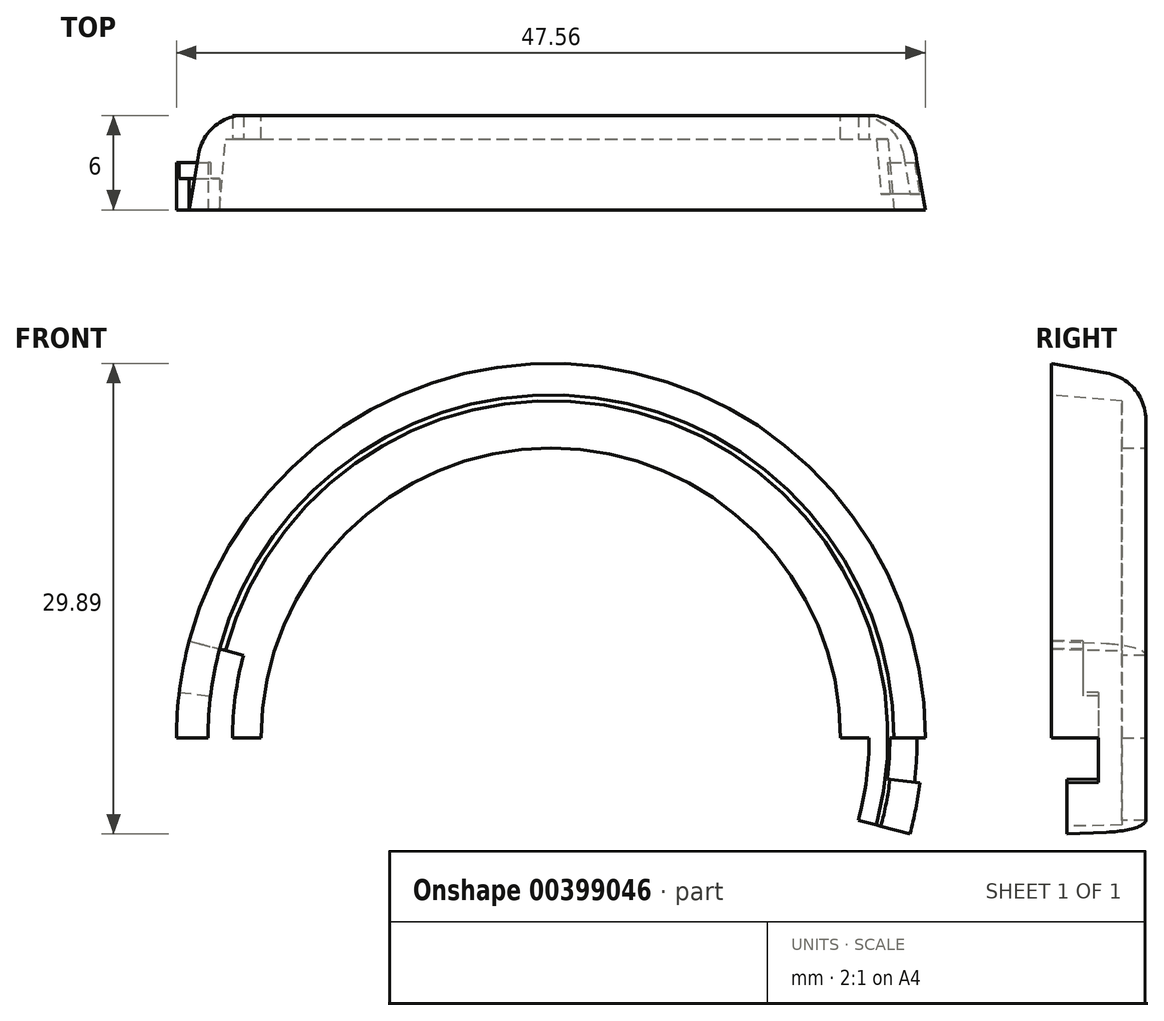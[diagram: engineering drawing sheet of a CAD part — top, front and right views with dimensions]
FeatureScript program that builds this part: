
annotation { "Feature Type Name" : "Feature", "Feature Type Description" : "" }
export const myFeature = defineFeature(function(context is Context, id is Id, definition is map)
    precondition{}
    {
        {
            var Q0;
            Q0=qCreatedBy(makeId("Top.planeOp"),FACE);
            var sketch = newSketch(context, id + "F0", { "sketchPlane" : qUnion([Q0])});
            skLineSegment(sketch, "E0", {"start": v(0, 0) * mm, "end": v(0, -13.08) * mm, "construction": true});
            skLineSegment(sketch, "E1", {"start": v(18.4, 6) * mm, "end": v(18.4, 4.5) * mm});
            skLineSegment(sketch, "E2", {"start": v(18.4, 6) * mm, "end": v(22.74, 6) * mm});
            skLineSegment(sketch, "E3", {"start": v(22.74, 6) * mm, "end": v(23.78, 0) * mm});
            skLineSegment(sketch, "E4", {"start": v(23.78, 0) * mm, "end": v(21.78, 0) * mm});
            skLineSegment(sketch, "E5", {"start": v(21.78, 0) * mm, "end": v(21.4, 4.5) * mm});
            skLineSegment(sketch, "E6", {"start": v(21.4, 4.5) * mm, "end": v(18.4, 4.5) * mm});
            skSolve(sketch);
        }
        {
            var Q0;
            Q0 = qSketchRegion(id + "F0", true);
            var Q1;
            Q1=sQuery(id+"F0.wireOp",EDGE,"E0");
            revolve(context, id + "F1", {"entities" : qUnion([Q0]), "axis" : qUnion([Q1]), "revolveType" : RevolveType.FULL});
        }
        {
            var Q0;
            Q0=makeQuery(id+"F1.opRevolve","SWEPT_EDGE",EDGE,{"disambiguationData":[OSD([sQuery(id+"F0.wireOp",EDGE,"E2"),sQuery(id+"F0.wireOp",EDGE,"E3")])]});
            fillet(context, id + "F2", {"entities" : qUnion([Q0]), "radius" : 3 * mm, "tangentPropagation" : true, "allowEdgeOverflow" : false});
        }
        {
            var Q0;
            Q0=qCreatedBy(makeId("Front.planeOp"),FACE);
            var sketch = newSketch(context, id + "F3", { "sketchPlane" : qUnion([Q0])});
            skLineSegment(sketch, "E7", {"start": v(-26.64, 7.14) * mm, "end": v(-19.53, 5.23) * mm});
            skLineSegment(sketch, "E8", {"start": v(-20.21, 0) * mm, "end": v(0, 0) * mm});
            skLineSegment(sketch, "E9", {"start": v(0, 0) * mm, "end": v(20.21, 0) * mm});
            skLineSegment(sketch, "E10", {"start": v(19.53, -5.23) * mm, "end": v(26.77, -7.17) * mm});
            skLineSegment(sketch, "E11", {"start": v(-26.64, 7.14) * mm, "end": v(-26.64, -27.7) * mm});
            skLineSegment(sketch, "E12", {"start": v(-26.64, -27.7) * mm, "end": v(26.77, -27.7) * mm});
            skLineSegment(sketch, "E13", {"start": v(26.77, -27.7) * mm, "end": v(26.77, -7.17) * mm});
            skLineSegment(sketch, "E14", {"start": v(-19.53, 5.23) * mm, "end": v(0, 0) * mm, "construction": true});
            skArc(sketch, "E15", {"start": v(-19.53, 5.23) * mm, "mid": v(-20.04, 2.64) * mm, "end": v(-20.21, 0) * mm});
            skLineSegment(sketch, "E16", {"start": v(0, 0) * mm, "end": v(19.53, -5.23) * mm, "construction": true});
            skArc(sketch, "E17", {"start": v(19.53, -5.23) * mm, "mid": v(20.04, -2.64) * mm, "end": v(20.21, 0) * mm});
            skSolve(sketch);
        }
        {
            var Q0;
            Q0 = qSketchRegion(id + "F3", true);
            extrude(context, id + "F4", {"entities" : qUnion([Q0]), "operationType" : NewBodyOperationType.REMOVE, "oppositeDirection" : true, "depth" : 25 * mm});
        }
        {
            var Q0;
            Q0=makeQuery(id+"F1.opRevolve","SWEPT_FACE",FACE,{"disambiguationData":[OSD([sQuery(id+"F0.wireOp",EDGE,"E4")])]});
            var sketch = newSketch(context, id + "F5", { "sketchPlane" : qUnion([Q0])});
            skLineSegment(sketch, "E18", {"start": v(0, 0) * mm, "end": v(23.8, 0) * mm});
            skLineSegment(sketch, "E19", {"start": v(0, 0) * mm, "end": v(24.13, -2.96) * mm});
            skLineSegment(sketch, "E20", {"start": v(24.13, -2.96) * mm, "end": v(23.8, 0) * mm});
            skSolve(sketch);
        }
        {
            var Q0;
            Q0 = qSketchRegion(id + "F5", true);
            extrude(context, id + "F6", {"entities" : qUnion([Q0]), "operationType" : NewBodyOperationType.REMOVE, "oppositeDirection" : true, "depth" : 3 * mm});
        }
        {
            var Q0;
            Q0=makeQuery(id+"F6.boolean.opBoolean","SPLIT",FACE,{"disambiguationData":[TD([makeQuery(id+"F4.boolean.opBoolean","COPY",FACE,{"derivedFrom":makeQuery(id+"F4.opExtrude","SWEPT_FACE",FACE,{"disambiguationData":[OSD([sQuery(id+"F3.wireOp",EDGE,"E10")])]})})])],"derivedFrom":makeQuery(id+"F1.opRevolve","SWEPT_FACE",FACE,{"disambiguationData":[OSD([sQuery(id+"F0.wireOp",EDGE,"E4")])]})});
            var sketch = newSketch(context, id + "F7", { "sketchPlane" : qUnion([Q0])});
            skLineSegment(sketch, "E21", {"start": v(18.03, -5.95) * mm, "end": v(23.6, -7.73) * mm});
            skLineSegment(sketch, "E22", {"start": v(23.6, -7.73) * mm, "end": v(24.28, -2.47) * mm});
            skLineSegment(sketch, "E23", {"start": v(24.28, -2.47) * mm, "end": v(18.75, -1.71) * mm});
            skLineSegment(sketch, "E24", {"start": v(18.75, -1.71) * mm, "end": v(18.03, -5.95) * mm});
            skSolve(sketch);
        }
        {
            var Q0;
            Q0 = qSketchRegion(id + "F7", true);
            extrude(context, id + "F8", {"entities" : qUnion([Q0]), "operationType" : NewBodyOperationType.REMOVE, "oppositeDirection" : true, "depth" : 1 * mm});
        }
        {
            var Q0;
            Q0=makeQuery(id+"F6.boolean.opBoolean","SPLIT",FACE,{"disambiguationData":[TD([makeQuery(id+"F4.boolean.opBoolean","COPY",FACE,{"derivedFrom":makeQuery(id+"F4.opExtrude","SWEPT_FACE",FACE,{"disambiguationData":[OSD([sQuery(id+"F3.wireOp",EDGE,"E7")])]})})])],"derivedFrom":makeQuery(id+"F1.opRevolve","SWEPT_FACE",FACE,{"disambiguationData":[OSD([sQuery(id+"F0.wireOp",EDGE,"E4")])]})});
            var sketch = newSketch(context, id + "F9", { "sketchPlane" : qUnion([Q0])});
            skArc(sketch, "E25", {"start": v(-22.97, 6.15) * mm, "mid": v(-23.58, 3.1) * mm, "end": v(-23.78, 0) * mm});
            skArc(sketch, "E26", {"start": v(-21.04, 5.64) * mm, "mid": v(-21.6, 2.84) * mm, "end": v(-21.78, 0) * mm});
            skLineSegment(sketch, "E27", {"start": v(-23.78, 0) * mm, "end": v(-21.78, 0) * mm});
            skLineSegment(sketch, "E28", {"start": v(-21.04, 5.64) * mm, "end": v(-22.97, 6.15) * mm});
            skSolve(sketch);
        }
        {
            var Q0;
            Q0 = qSketchRegion(id + "F9", true);
            extrude(context, id + "F10", {"entities" : qUnion([Q0]), "operationType" : NewBodyOperationType.ADD, "oppositeDirection" : true, "depth" : 2 * mm});
        }
        {
            var Q0;
            Q0=makeQuery(id+"F10.opExtrude","CAP_FACE",FACE,{"disambiguationData":[OSD([sQuery(id+"F9.wireOp",EDGE,"E25"),sQuery(id+"F9.wireOp",EDGE,"E26"),sQuery(id+"F9.wireOp",EDGE,"E27"),sQuery(id+"F9.wireOp",EDGE,"E28")])],"isStart":false});
            var sketch = newSketch(context, id + "F11", { "sketchPlane" : qUnion([Q0])});
            skArc(sketch, "E29", {"start": v(23.78, 0) * mm, "mid": v(23.74, 1.45) * mm, "end": v(23.6, 2.9) * mm});
            skArc(sketch, "E30", {"start": v(21.78, 0) * mm, "mid": v(21.74, 1.33) * mm, "end": v(21.62, 2.65) * mm});
            skLineSegment(sketch, "E31", {"start": v(21.78, 0) * mm, "end": v(23.78, 0) * mm});
            skLineSegment(sketch, "E32", {"start": v(23.6, 2.9) * mm, "end": v(21.62, 2.65) * mm});
            skLineSegment(sketch, "E33", {"start": v(21.62, 2.65) * mm, "end": v(0, 0) * mm, "construction": true});
            skLineSegment(sketch, "E34", {"start": v(21.78, 0) * mm, "end": v(0, 0) * mm, "construction": true});
            skSolve(sketch);
        }
        {
            var Q0;
            Q0 = qSketchRegion(id + "F11", true);
            extrude(context, id + "F12", {"entities" : qUnion([Q0]), "operationType" : NewBodyOperationType.ADD, "depth" : 1 * mm});
        }
    });
